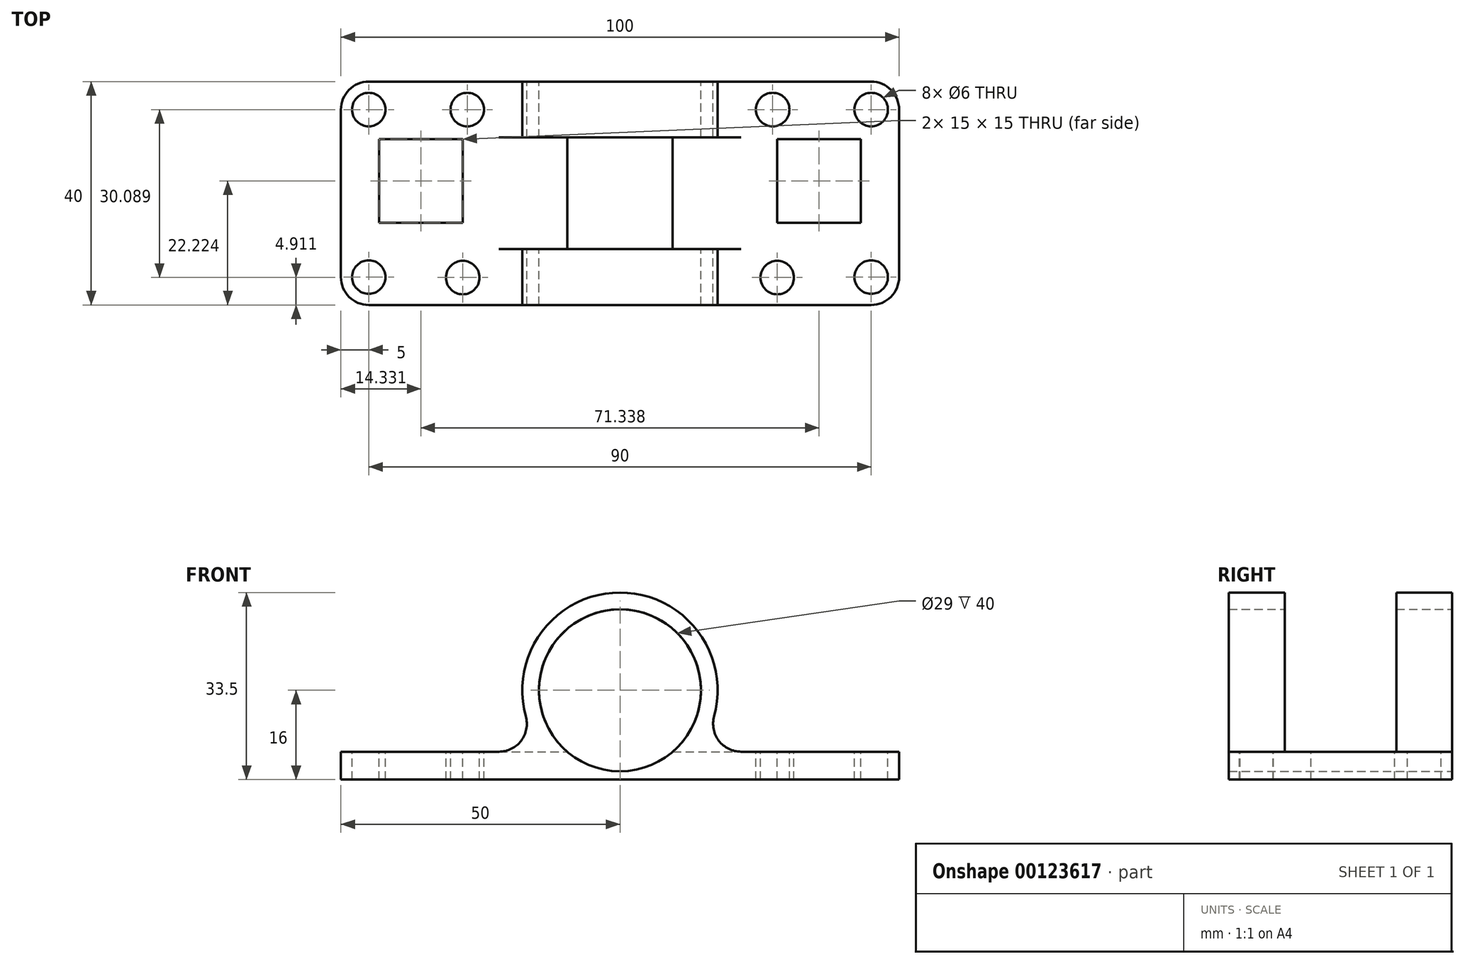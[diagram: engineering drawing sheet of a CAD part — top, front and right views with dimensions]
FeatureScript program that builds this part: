
annotation { "Feature Type Name" : "Feature", "Feature Type Description" : "" }
export const myFeature = defineFeature(function(context is Context, id is Id, definition is map)
    precondition{}
    {
        {
            var Q0;
            Q0=qCreatedBy(makeId("Front.planeOp"),FACE);
            var sketch = newSketch(context, id + "F0", { "sketchPlane" : qUnion([Q0])});
            skCircle(sketch, "E0", {"center": v(0, 0) * mm, "radius": 14.5 * mm});
            skLineSegment(sketch, "E1.bottom", {"start": v(-50, -11) * mm, "end": v(-13.61, -11) * mm});
            skLineSegment(sketch, "E1.top", {"start": v(-50, -16) * mm, "end": v(50, -16) * mm});
            skLineSegment(sketch, "E1.left", {"start": v(-50, -11) * mm, "end": v(-50, -16) * mm});
            skLineSegment(sketch, "E1.right", {"start": v(50, -11) * mm, "end": v(50, -16) * mm});
            skArc(sketch, "E2", {"start": v(13.61, -11) * mm, "mid": v(0, 17.5) * mm, "end": v(-13.61, -11) * mm});
            skLineSegment(sketch, "E3.trimOffspring", {"start": v(13.61, -11) * mm, "end": v(50, -11) * mm});
            skSolve(sketch);
        }
        {
            var Q0;
            Q0=makeQuery(id+"F0.imprint","IMPRINT",FACE,{"disambiguationData":[TD([[makeQuery(id+"F0.imprint","IMPRINT",EDGE,{"derivedFrom":sQuery(id+"F0.wireOp",EDGE,"E0")}),-1.0]])]});
            extrude(context, id + "F1", {"entities" : qUnion([Q0]), "depth" : 40 * mm});
        }
        {
            var Q0;
            Q0=makeQuery(id+"F1.opExtrude","SWEPT_EDGE",EDGE,{"disambiguationData":[OSD([sQuery(id+"F0.wireOp",EDGE,"E2"),sQuery(id+"F0.wireOp",EDGE,"E3.trimOffspring")])]});
            var Q1;
            Q1=makeQuery(id+"F1.opExtrude","SWEPT_EDGE",EDGE,{"disambiguationData":[OSD([sQuery(id+"F0.wireOp",EDGE,"E1.bottom"),sQuery(id+"F0.wireOp",EDGE,"E2")])]});
            fillet(context, id + "F2", {"entities" : qUnion([Q0, Q1]), "radius" : 5 * mm, "tangentPropagation" : true, "allowEdgeOverflow" : false});
        }
        {
            var Q0;
            Q0=makeQuery(id+"F1.opExtrude","CAP_EDGE",EDGE,{"disambiguationData":[OSD([sQuery(id+"F0.wireOp",EDGE,"E1.right")])],"isStart":false});
            var Q1;
            Q1=makeQuery(id+"F1.opExtrude","CAP_EDGE",EDGE,{"disambiguationData":[OSD([sQuery(id+"F0.wireOp",EDGE,"E1.left")])],"isStart":false});
            var Q2;
            Q2=makeQuery(id+"F1.opExtrude","CAP_EDGE",EDGE,{"disambiguationData":[OSD([sQuery(id+"F0.wireOp",EDGE,"E1.right")])],"isStart":true});
            var Q3;
            Q3=makeQuery(id+"F1.opExtrude","CAP_EDGE",EDGE,{"disambiguationData":[OSD([sQuery(id+"F0.wireOp",EDGE,"E1.left")])],"isStart":true});
            fillet(context, id + "F3", {"entities" : qUnion([Q0, Q1, Q2, Q3]), "radius" : 5 * mm, "tangentPropagation" : true, "allowEdgeOverflow" : false});
        }
        {
            var Q0;
            Q0=makeQuery(id+"F1.opExtrude","SWEPT_FACE",FACE,{"disambiguationData":[OSD([sQuery(id+"F0.wireOp",EDGE,"E1.bottom")])]});
            var sketch = newSketch(context, id + "F4", { "sketchPlane" : qUnion([Q0])});
            skLineSegment(sketch, "E4.bottom", {"start": v(-43.17, -10.28) * mm, "end": v(-28.17, -10.28) * mm});
            skLineSegment(sketch, "E4.top", {"start": v(-43.17, -25.28) * mm, "end": v(-28.17, -25.28) * mm});
            skLineSegment(sketch, "E4.left", {"start": v(-43.17, -10.28) * mm, "end": v(-43.17, -25.28) * mm});
            skLineSegment(sketch, "E4.right", {"start": v(-28.17, -10.28) * mm, "end": v(-28.17, -25.28) * mm});
            skPoint(sketch, "E4.middle", {"position": v(-35.67, -17.78) * mm});
            skCircle(sketch, "E5", {"center": v(-45, -5) * mm, "radius": 3 * mm});
            skCircle(sketch, "E6", {"center": v(-27.36, -5) * mm, "radius": 3 * mm});
            skCircle(sketch, "E7", {"center": v(-45, -35) * mm, "radius": 3 * mm});
            skCircle(sketch, "E8", {"center": v(-28.17, -35.09) * mm, "radius": 3 * mm});
            skSolve(sketch);
        }
        {
            var Q0;
            Q0=makeQuery(id+"F4.imprint","IMPRINT",FACE,{"disambiguationData":[TD([[makeQuery(id+"F4.imprint","IMPRINT",EDGE,{"derivedFrom":sQuery(id+"F4.wireOp",EDGE,"E4.bottom")}),-1.0]])]});
            var Q1;
            Q1=makeQuery(id+"F4.imprint","IMPRINT",FACE,{"disambiguationData":[TD([[makeQuery(id+"F4.imprint","IMPRINT",EDGE,{"derivedFrom":sQuery(id+"F4.wireOp",EDGE,"E7")}),1.0]])]});
            var Q2;
            Q2=makeQuery(id+"F4.imprint","IMPRINT",FACE,{"disambiguationData":[TD([[makeQuery(id+"F4.imprint","IMPRINT",EDGE,{"derivedFrom":sQuery(id+"F4.wireOp",EDGE,"E8")}),1.0]])]});
            var Q3;
            Q3=makeQuery(id+"F4.imprint","IMPRINT",FACE,{"disambiguationData":[TD([[makeQuery(id+"F4.imprint","IMPRINT",EDGE,{"derivedFrom":sQuery(id+"F4.wireOp",EDGE,"E5")}),1.0]])]});
            var Q4;
            Q4=makeQuery(id+"F4.imprint","IMPRINT",FACE,{"disambiguationData":[TD([[makeQuery(id+"F4.imprint","IMPRINT",EDGE,{"derivedFrom":sQuery(id+"F4.wireOp",EDGE,"E6")}),1.0]])]});
            extrude(context, id + "F5", {"entities" : qUnion([Q0, Q1, Q2, Q3, Q4]), "operationType" : NewBodyOperationType.REMOVE, "oppositeDirection" : true, "depth" : 25 * mm});
        }
        {
            var Q0;
            Q0=qCreatedBy(makeId("Right.planeOp"),FACE);
            var sketch = newSketch(context, id + "F6", { "sketchPlane" : qUnion([Q0])});
            skLineSegment(sketch, "E9.bottom", {"start": v(33.8, 29.22) * mm, "end": v(-76.46, 29.22) * mm});
            skLineSegment(sketch, "E9.top", {"start": v(33.8, -41.93) * mm, "end": v(-76.46, -41.93) * mm});
            skLineSegment(sketch, "E9.left", {"start": v(33.8, 29.22) * mm, "end": v(33.8, -41.93) * mm});
            skLineSegment(sketch, "E9.right", {"start": v(-76.46, 29.22) * mm, "end": v(-76.46, -41.93) * mm});
            skSolve(sketch);
        }
        {
            var Q0;
            Q0=makeQuery(id+"F6.imprint","IMPRINT",FACE,{"disambiguationData":[TD([[makeQuery(id+"F6.imprint","IMPRINT",EDGE,{"derivedFrom":sQuery(id+"F6.wireOp",EDGE,"E9.bottom")}),1.0]])]});
            extrude(context, id + "F7", {"entities" : qUnion([Q0]), "operationType" : NewBodyOperationType.REMOVE, "endBound" : BoundingType.THROUGH_ALL, "depth" : 25 * mm});
        }
        {
            var Q0;
            Q0=makeQuery(id+"F1.opExtrude","SWEPT_BODY",BODY,{"disambiguationData":[OSD([sQuery(id+"F0.wireOp",EDGE,"E0"),sQuery(id+"F0.wireOp",EDGE,"E1.bottom"),sQuery(id+"F0.wireOp",EDGE,"E1.top"),sQuery(id+"F0.wireOp",EDGE,"E1.left"),sQuery(id+"F0.wireOp",EDGE,"E1.right"),sQuery(id+"F0.wireOp",EDGE,"E2"),sQuery(id+"F0.wireOp",EDGE,"E3.trimOffspring")])]});
            var Q1;
            Q1=qCreatedBy(makeId("Right.planeOp"),FACE);
            mirror(context, id + "F8", {"operationType" : NewBodyOperationType.ADD, "entities" : qUnion([Q0]), "mirrorPlane" : qUnion([Q1])});
        }
        {
            var Q0;
            Q0=makeQuery(id+"F1.opExtrude","SWEPT_FACE",FACE,{"disambiguationData":[OSD([sQuery(id+"F0.wireOp",EDGE,"E1.bottom")])]});
            var sketch = newSketch(context, id + "F9", { "sketchPlane" : qUnion([Q0])});
            skLineSegment(sketch, "E10.bottom", {"start": v(-31.67, -10) * mm, "end": v(28.23, -10) * mm});
            skLineSegment(sketch, "E10.top", {"start": v(-31.67, -30) * mm, "end": v(28.23, -30) * mm});
            skLineSegment(sketch, "E10.left", {"start": v(-31.67, -10) * mm, "end": v(-31.67, -30) * mm});
            skLineSegment(sketch, "E10.right", {"start": v(28.23, -10) * mm, "end": v(28.23, -30) * mm});
            skSolve(sketch);
        }
        {
            var Q0;
            {var subQ6=sQuery(id+"F4.wireOp",EDGE,"E4.right");var subQ16=makeQuery(id+"F5.boolean.opBoolean","COPY",EDGE,{"derivedFrom":makeQuery(id+"F5.opExtrude","CAP_EDGE",EDGE,{"disambiguationData":[OSD([subQ6])],"isStart":true})});Q0=makeQuery(id+"F9.imprint","IMPRINT",FACE,{"disambiguationData":[TD([[makeQuery(id+"F9.imprint","IMPRINT",EDGE,{"derivedFrom":subQ16}),1.0]])]});}
            var Q1;
            {var subQ0=sQuery(id+"F9.wireOp",EDGE,"E10.right");Q1=makeQuery(id+"F9.imprint","IMPRINT",FACE,{"disambiguationData":[TD([[makeQuery(id+"F9.imprint","IMPRINT",EDGE,{"derivedFrom":subQ0}),-1.0]])]});}
            extrude(context, id + "F10", {"entities" : qUnion([Q0, Q1]), "operationType" : NewBodyOperationType.REMOVE, "endBound" : BoundingType.THROUGH_ALL, "depth" : 25 * mm});
        }
    });
